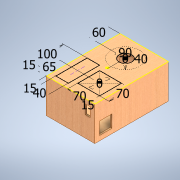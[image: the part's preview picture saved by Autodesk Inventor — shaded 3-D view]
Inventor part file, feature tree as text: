
AUTODESK INVENTOR PART (.ipt)
format: ipt  version: 2022 (Build 260153000, 153)  size: 206,336 bytes
history: native  units: mm
features: extrude x7, sketch x6, shell x1
ambient origin geometry x8: Origin, YZ Plane, XZ Plane, XY Plane, X Axis, Y Axis, Z Axis, Center Point
bodies: Solid1 (feature_tree)
feature tree (14):
  extrude  "Extrusion1"  Depth=155.0mm
  shell  "Shell1"  Thickness=110.0mm
  extrude  "Extrusion2"  Depth=5.0mm
  sketch  "Sketch3"  dims[d6=130.0mm d7=0.0mm d12=70.0mm]
  sketch  "Sketch4"  dims[d13=70.0mm d20=40.0mm]
  sketch  "Sketch5"  dims[d23=40.0mm d24=40.0mm]
  extrude  "Extrusion3"  Depth=70.0mm
  extrude  "Extrusion4"  Depth=40.0mm
  extrude  "Extrusion5"  Depth=40.0mm
  extrude  "Extrusion6"  Depth=15.0mm
  extrude  "Extrusion7"  Depth=30.0mm
  sketch  "Sketch1"  dims[d0=235.0mm d1=155.0mm d2=110.0mm d3=0.0mm]
  sketch  "Sketch2"  dims[d4=5.0mm d5=5.0mm]
  sketch  "Sketch6"  dims[d25=15.0mm d26=15.0mm d27=30.0mm d28=15.0mm d29=15.0mm d30=15.0mm d31=15.0mm d32=100.0mm d33=40.0mm d34=15.0mm d35=15.0mm d37=0.0mm d38=65.0mm d40=0.0mm d41=60.0mm d42=90.0mm d44=100.0mm d45=5.0mm d46=0.0mm d47=0.0mm d48=10.0mm d49=0.0mm d50=10.0mm d51=0.0mm d52=10.0mm d53=0.0mm d55=0.1mm d56=0.0mm]
